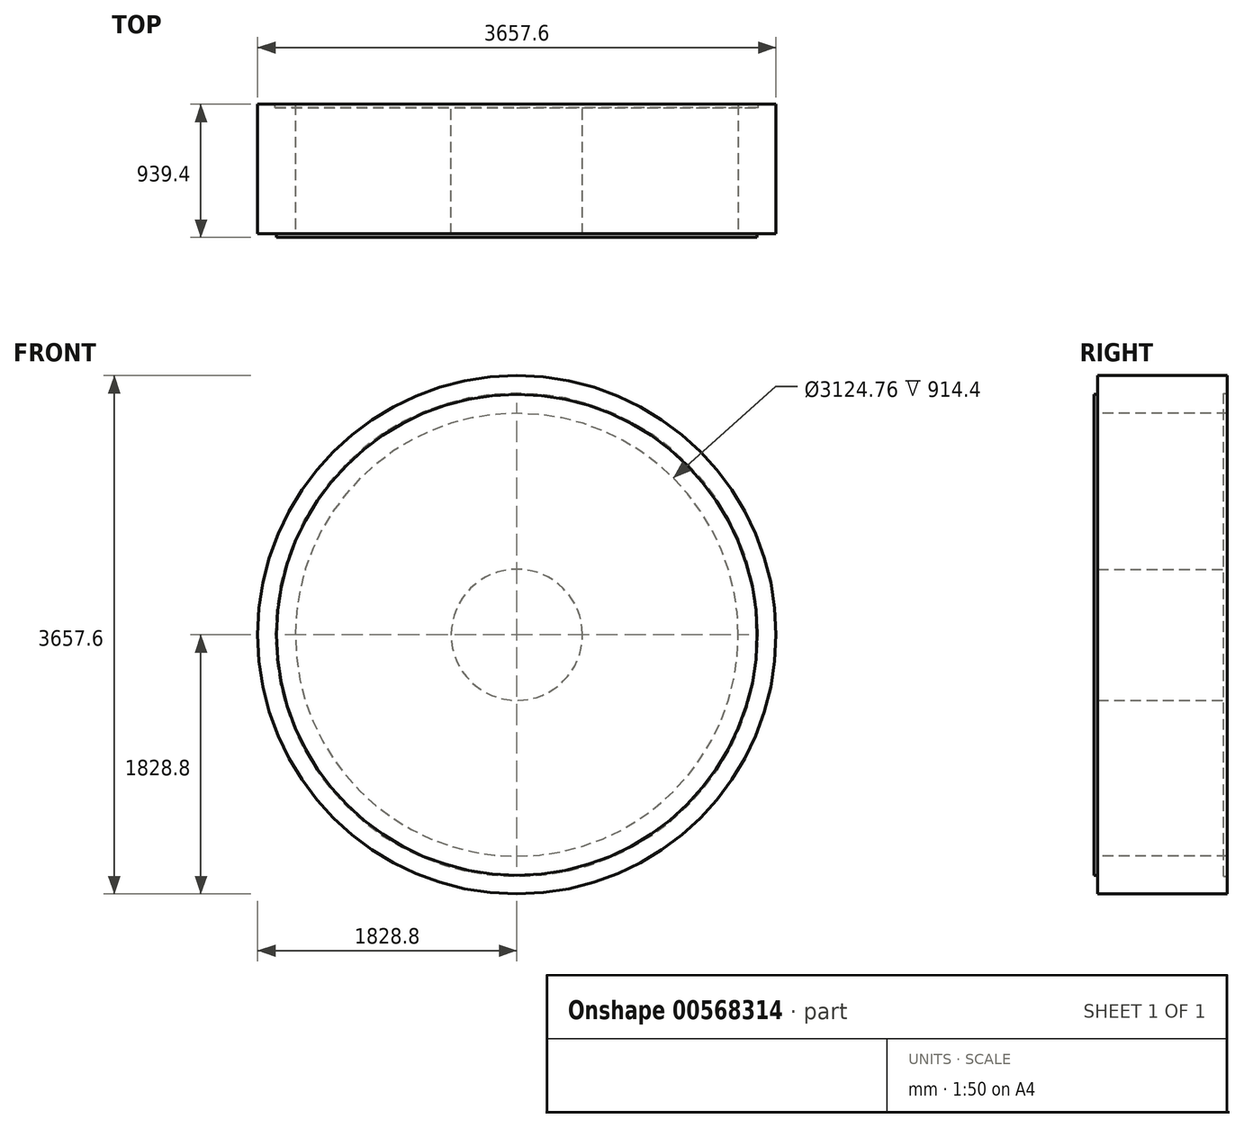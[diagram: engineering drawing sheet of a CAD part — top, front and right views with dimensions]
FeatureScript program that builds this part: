
annotation { "Feature Type Name" : "Feature", "Feature Type Description" : "" }
export const myFeature = defineFeature(function(context is Context, id is Id, definition is map)
    precondition{}
    {
        {
            var Q0;
            Q0=qCreatedBy(makeId("Front.planeOp"),FACE);
            var sketch = newSketch(context, id + "F0", { "sketchPlane" : qUnion([Q0])});
            skCircle(sketch, "E0", {"center": v(0, 0) * mm, "radius": 1828.8 * mm});
            skSolve(sketch);
        }
        {
            var Q0;
            Q0=makeQuery(id+"F0.imprint","IMPRINT",FACE,{"disambiguationData":[TD([[makeQuery(id+"F0.imprint","IMPRINT",EDGE,{"derivedFrom":sQuery(id+"F0.wireOp",EDGE,"E0")}),1.0]])]});
            var sketch = newSketch(context, id + "F1", { "sketchPlane" : qUnion([Q0])});
            skSolve(sketch);
        }
        {
            var Q0;
            Q0=makeQuery(id+"F1.imprint","IMPRINT",FACE,{"disambiguationData":[TD([[makeQuery(id+"F1.imprint","IMPRINT",EDGE,{"derivedFrom":makeQuery(id+"F0.imprint","IMPRINT",EDGE,{"derivedFrom":sQuery(id+"F0.wireOp",EDGE,"E0")})}),1.0]])]});
            extrude(context, id + "F2", {"entities" : qUnion([Q0]), "depth" : 914.4 * mm, "offsetDistance" : 25 * mm});
        }
        {
            var Q0;
            Q0=makeQuery(id+"F2.opExtrude","CAP_FACE",FACE,{"disambiguationData":[OSD([sQuery(id+"F0.wireOp",EDGE,"E0")])],"isStart":false});
            var sketch = newSketch(context, id + "F3", { "sketchPlane" : qUnion([Q0])});
            skCircle(sketch, "E1", {"center": v(0, 0) * mm, "radius": 1562.38 * mm});
            skSolve(sketch);
        }
        {
            var Q0;
            Q0=makeQuery(id+"F3.imprint","IMPRINT",FACE,{"disambiguationData":[TD([[makeQuery(id+"F3.imprint","IMPRINT",EDGE,{"derivedFrom":sQuery(id+"F3.wireOp",EDGE,"E1")}),1.0]])]});
            extrude(context, id + "F4", {"entities" : qUnion([Q0]), "operationType" : NewBodyOperationType.REMOVE, "endBound" : BoundingType.THROUGH_ALL, "oppositeDirection" : true, "depth" : 25 * mm, "offsetDistance" : 25 * mm});
        }
        {
            var Q0;
            Q0 = qSketchRegion(id + "F0", true);
            var sketch = newSketch(context, id + "F5", { "sketchPlane" : qUnion([Q0])});
            skCircle(sketch, "E2", {"center": v(0, 0) * mm, "radius": 462.99 * mm});
            skSolve(sketch);
        }
        {
            var Q0;
            Q0 = qSketchRegion(id + "F5", true);
            extrude(context, id + "F6", {"entities" : qUnion([Q0]), "depth" : 914.4 * mm, "offsetDistance" : 25 * mm});
        }
        {
            var Q0;
            Q0=makeQuery(id+"F6.opExtrude","CAP_FACE",FACE,{"disambiguationData":[OSD([sQuery(id+"F5.wireOp",EDGE,"E2")])],"isStart":false});
            var sketch = newSketch(context, id + "F7", { "sketchPlane" : qUnion([Q0])});
            skCircle(sketch, "E3", {"center": v(0, 0) * mm, "radius": 1695.83 * mm});
            skSolve(sketch);
        }
        {
            var Q0;
            Q0 = qSketchRegion(id + "F7", true);
            extrude(context, id + "F8", {"entities" : qUnion([Q0]), "depth" : 25 * mm, "offsetDistance" : 25 * mm});
        }
        {
            var Q0;
            Q0=makeQuery(id+"F0.imprint","IMPRINT",FACE,{"disambiguationData":[TD([[makeQuery(id+"F0.imprint","IMPRINT",EDGE,{"derivedFrom":sQuery(id+"F0.wireOp",EDGE,"E0")}),1.0]])]});
            var sketch = newSketch(context, id + "F9", { "sketchPlane" : qUnion([Q0])});
            skCircle(sketch, "E4", {"center": v(0, 0) * mm, "radius": 1704.53 * mm});
            skSolve(sketch);
        }
        {
            var Q0;
            Q0 = qSketchRegion(id + "F9", true);
            extrude(context, id + "F10", {"entities" : qUnion([Q0]), "depth" : 25 * mm, "offsetDistance" : 25 * mm});
        }
    });
